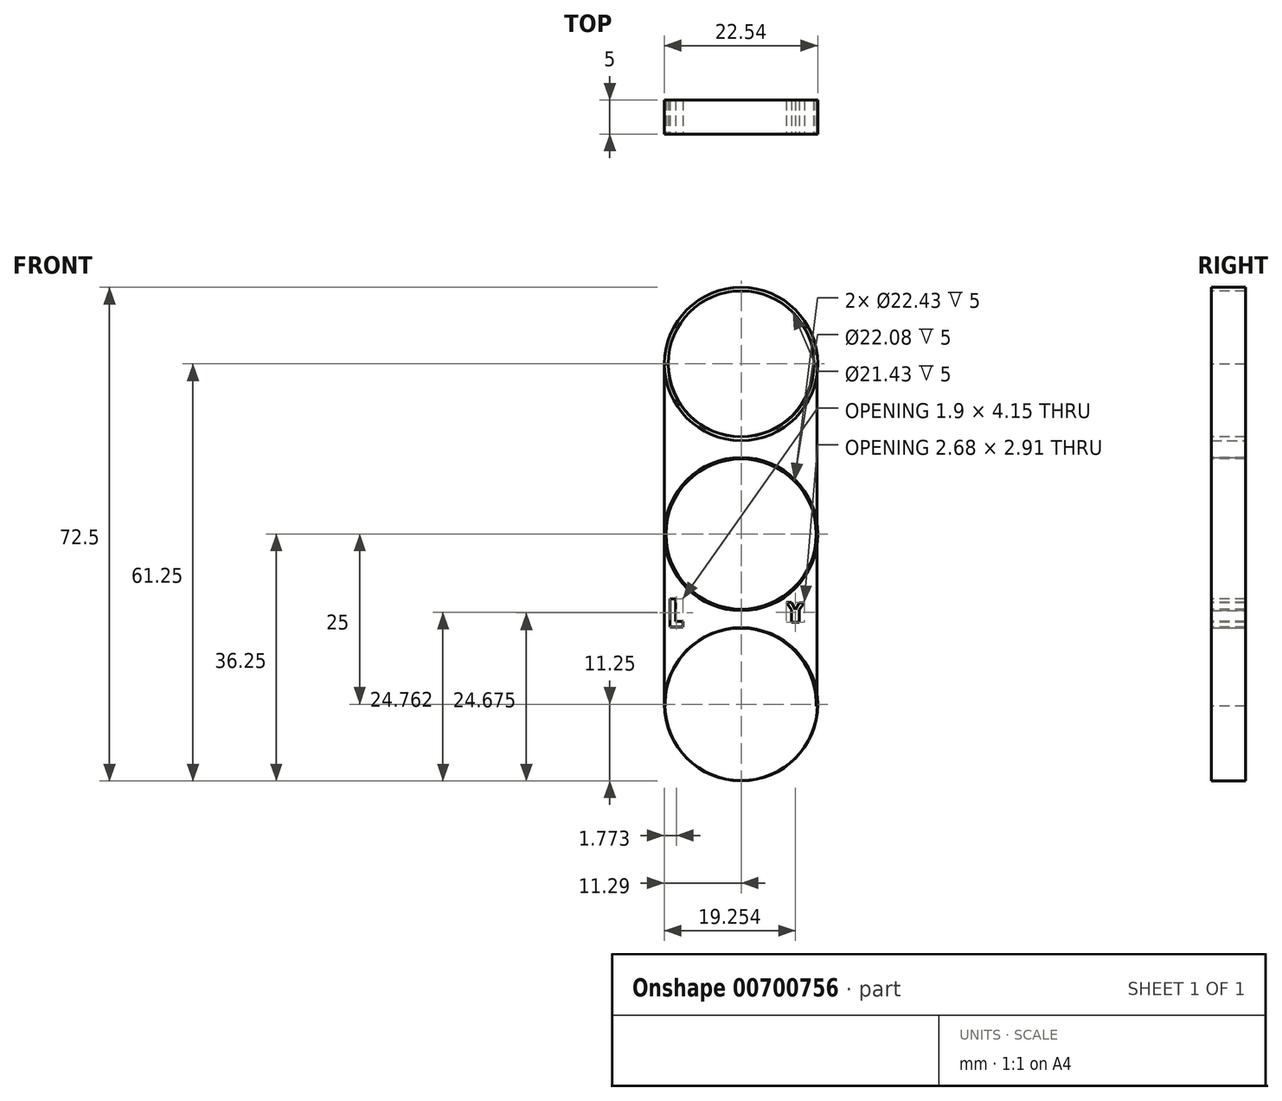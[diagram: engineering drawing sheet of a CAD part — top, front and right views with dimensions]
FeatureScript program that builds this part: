
annotation { "Feature Type Name" : "Feature", "Feature Type Description" : "" }
export const myFeature = defineFeature(function(context is Context, id is Id, definition is map)
    precondition{}
    {
        {
            var Q0;
            Q0=qCreatedBy(makeId("Front.planeOp"),FACE);
            var sketch = newSketch(context, id + "F0", { "sketchPlane" : qUnion([Q0])});
            skCircle(sketch, "E0", {"center": v(0, 25) * mm, "radius": 11.25 * mm});
            skCircle(sketch, "E1", {"center": v(0, 0) * mm, "radius": 11.25 * mm});
            skCircle(sketch, "E2", {"center": v(0, -25) * mm, "radius": 11.25 * mm});
            skSolve(sketch);
        }
        {
            var Q0;
            Q0=makeQuery(id+"F0.imprint","IMPRINT",FACE,{"disambiguationData":[TD([[makeQuery(id+"F0.imprint","IMPRINT",EDGE,{"derivedFrom":sQuery(id+"F0.wireOp",EDGE,"E0")}),1.0]])]});
            var Q1;
            Q1=makeQuery(id+"F0.imprint","IMPRINT",FACE,{"disambiguationData":[TD([[makeQuery(id+"F0.imprint","IMPRINT",EDGE,{"derivedFrom":sQuery(id+"F0.wireOp",EDGE,"E1")}),1.0]])]});
            var Q2;
            Q2=makeQuery(id+"F0.imprint","IMPRINT",FACE,{"disambiguationData":[TD([[makeQuery(id+"F0.imprint","IMPRINT",EDGE,{"derivedFrom":sQuery(id+"F0.wireOp",EDGE,"E2")}),1.0]])]});
            extrude(context, id + "F1", {"entities" : qUnion([Q0, Q1, Q2]), "depth" : 5 * mm, "offsetDistance" : 25 * mm});
        }
        {
            var Q0;
            Q0=makeQuery(id+"F1.opExtrude","CAP_FACE",FACE,{"disambiguationData":[OSD([sQuery(id+"F0.wireOp",EDGE,"E0")])],"isStart":false});
            var sketch = newSketch(context, id + "F2", { "sketchPlane" : qUnion([Q0])});
            skCircle(sketch, "E3", {"center": v(0, 25) * mm, "radius": 10.71 * mm});
            skSolve(sketch);
        }
        {
            var Q0;
            Q0=qSketchRegion(id+"F2",true);
            extrude(context, id + "F3", {"entities" : qUnion([Q0]), "operationType" : NewBodyOperationType.REMOVE, "oppositeDirection" : true, "depth" : 25 * mm, "offsetDistance" : 25 * mm});
        }
        {
            var Q0;
            Q0=makeQuery(id+"F1.opExtrude","CAP_FACE",FACE,{"disambiguationData":[OSD([sQuery(id+"F0.wireOp",EDGE,"E1")])],"isStart":false});
            var sketch = newSketch(context, id + "F4", { "sketchPlane" : qUnion([Q0])});
            skCircle(sketch, "E4", {"center": v(0, 0) * mm, "radius": 11.21 * mm});
            skSolve(sketch);
        }
        {
            var Q0;
            Q0=qSketchRegion(id+"F4",true);
            extrude(context, id + "F5", {"entities" : qUnion([Q0]), "operationType" : NewBodyOperationType.REMOVE, "oppositeDirection" : true, "depth" : 25 * mm, "offsetDistance" : 25 * mm});
        }
        {
            var Q0;
            Q0=makeQuery(id+"F1.opExtrude","CAP_FACE",FACE,{"disambiguationData":[OSD([sQuery(id+"F0.wireOp",EDGE,"E2")])],"isStart":false});
            var sketch = newSketch(context, id + "F6", { "sketchPlane" : qUnion([Q0])});
            skCircle(sketch, "E5", {"center": v(0, -25) * mm, "radius": 11.21 * mm});
            skSolve(sketch);
        }
        {
            var Q0;
            Q0=qSketchRegion(id+"F6",true);
            extrude(context, id + "F7", {"entities" : qUnion([Q0]), "operationType" : NewBodyOperationType.REMOVE, "oppositeDirection" : true, "depth" : 25 * mm, "offsetDistance" : 25 * mm});
        }
        {
            var Q0;
            Q0=qCreatedBy(makeId("Front.planeOp"),FACE);
            var sketch = newSketch(context, id + "F8", { "sketchPlane" : qUnion([Q0])});
            skLineSegment(sketch, "E6", {"start": v(-11.29, 24.95) * mm, "end": v(-11.29, -25.3) * mm});
            skLineSegment(sketch, "E7", {"start": v(11.15, 24.95) * mm, "end": v(11.15, -25.3) * mm});
            skLineSegment(sketch, "E8", {"start": v(-11.29, -25.3) * mm, "end": v(11.15, -25.3) * mm});
            skLineSegment(sketch, "E9", {"start": v(-11.29, 24.95) * mm, "end": v(11.15, 24.95) * mm});
            skSolve(sketch);
        }
        {
            var Q0;
            Q0=qSketchRegion(id+"F8",true);
            extrude(context, id + "F9", {"entities" : qUnion([Q0]), "depth" : 5 * mm, "offsetDistance" : 25 * mm});
        }
        {
            var Q0;
            Q0=makeQuery(id+"F9.opExtrude","CAP_FACE",FACE,{"disambiguationData":[OSD([sQuery(id+"F8.wireOp",EDGE,"E6"),sQuery(id+"F8.wireOp",EDGE,"E7"),sQuery(id+"F8.wireOp",EDGE,"E8"),sQuery(id+"F8.wireOp",EDGE,"E9")])],"isStart":false});
            var sketch = newSketch(context, id + "F10", { "sketchPlane" : qUnion([Q0])});
            skArc(sketch, "E10", {"start": v(-10.67, 24.95) * mm, "mid": v(-0.03, 14.3) * mm, "end": v(10.62, 24.95) * mm});
            skLineSegment(sketch, "E11", {"start": v(-10.67, 24.95) * mm, "end": v(10.62, 24.95) * mm});
            skSolve(sketch);
        }
        {
            var Q0;
            Q0=qSketchRegion(id+"F10",true);
            extrude(context, id + "F11", {"entities" : qUnion([Q0]), "operationType" : NewBodyOperationType.REMOVE, "oppositeDirection" : true, "depth" : 25 * mm, "offsetDistance" : 25 * mm});
        }
        {
            var Q0;
            Q0=makeQuery(id+"F9.opExtrude","CAP_FACE",FACE,{"disambiguationData":[OSD([sQuery(id+"F8.wireOp",EDGE,"E6"),sQuery(id+"F8.wireOp",EDGE,"E7"),sQuery(id+"F8.wireOp",EDGE,"E8"),sQuery(id+"F8.wireOp",EDGE,"E9")])],"isStart":false});
            var sketch = newSketch(context, id + "F12", { "sketchPlane" : qUnion([Q0])});
            skCircle(sketch, "E12", {"center": v(0, 0) * mm, "radius": 11.04 * mm});
            skSolve(sketch);
        }
        {
            var Q0;
            Q0=qSketchRegion(id+"F12",true);
            extrude(context, id + "F13", {"entities" : qUnion([Q0]), "operationType" : NewBodyOperationType.REMOVE, "oppositeDirection" : true, "depth" : 25 * mm, "offsetDistance" : 25 * mm});
        }
        {
            var Q0;
            Q0=makeQuery(id+"F9.opExtrude","CAP_FACE",FACE,{"disambiguationData":[OSD([sQuery(id+"F8.wireOp",EDGE,"E6"),sQuery(id+"F8.wireOp",EDGE,"E7"),sQuery(id+"F8.wireOp",EDGE,"E8"),sQuery(id+"F8.wireOp",EDGE,"E9")])],"isStart":false});
            var sketch = newSketch(context, id + "F14", { "sketchPlane" : qUnion([Q0])});
            skArc(sketch, "E13", {"start": v(11.02, -25.3) * mm, "mid": v(-0.07, -13.82) * mm, "end": v(-11.17, -25.3) * mm});
            skLineSegment(sketch, "E14", {"start": v(-11.17, -25.3) * mm, "end": v(11.02, -25.3) * mm});
            skSolve(sketch);
        }
        {
            var Q0;
            Q0=qSketchRegion(id+"F14",true);
            extrude(context, id + "F15", {"entities" : qUnion([Q0]), "operationType" : NewBodyOperationType.REMOVE, "oppositeDirection" : true, "depth" : 25 * mm, "offsetDistance" : 25 * mm});
        }
        {
            var Q0;
            Q0=makeQuery(id+"F9.opExtrude","CAP_FACE",FACE,{"disambiguationData":[OSD([sQuery(id+"F8.wireOp",EDGE,"E6"),sQuery(id+"F8.wireOp",EDGE,"E7"),sQuery(id+"F8.wireOp",EDGE,"E8"),sQuery(id+"F8.wireOp",EDGE,"E9")])],"isStart":false});
            var sketch = newSketch(context, id + "F16", { "sketchPlane" : qUnion([Q0])});
            skLineSegment(sketch, "E15", {"start": v(-10.47, -9.5) * mm, "end": v(-10.47, -13.65) * mm});
            skLineSegment(sketch, "E16", {"start": v(-10.47, -13.65) * mm, "end": v(-8.57, -13.65) * mm});
            skLineSegment(sketch, "E17", {"start": v(-8.57, -13.65) * mm, "end": v(-8.57, -12.82) * mm});
            skLineSegment(sketch, "E18", {"start": v(-8.57, -12.82) * mm, "end": v(-9.6, -12.82) * mm});
            skLineSegment(sketch, "E19", {"start": v(-9.6, -12.82) * mm, "end": v(-9.6, -9.5) * mm});
            skLineSegment(sketch, "E20", {"start": v(-9.6, -9.5) * mm, "end": v(-10.47, -9.5) * mm});
            skSolve(sketch);
        }
        {
            var Q0;
            Q0=qSketchRegion(id+"F16",true);
            extrude(context, id + "F17", {"entities" : qUnion([Q0]), "operationType" : NewBodyOperationType.REMOVE, "oppositeDirection" : true, "depth" : 25 * mm, "offsetDistance" : 25 * mm});
        }
        {
            var Q0;
            Q0=makeQuery(id+"F9.opExtrude","CAP_FACE",FACE,{"disambiguationData":[OSD([sQuery(id+"F8.wireOp",EDGE,"E6"),sQuery(id+"F8.wireOp",EDGE,"E7"),sQuery(id+"F8.wireOp",EDGE,"E8"),sQuery(id+"F8.wireOp",EDGE,"E9")])],"isStart":false});
            var sketch = newSketch(context, id + "F18", { "sketchPlane" : qUnion([Q0])});
            skLineSegment(sketch, "E21", {"start": v(6.62, -10.04) * mm, "end": v(7.4, -10.04) * mm});
            skLineSegment(sketch, "E22", {"start": v(7.4, -10.04) * mm, "end": v(7.96, -11.1) * mm});
            skLineSegment(sketch, "E23", {"start": v(7.96, -11.1) * mm, "end": v(8.52, -10.1) * mm});
            skLineSegment(sketch, "E24", {"start": v(8.52, -10.1) * mm, "end": v(9.3, -10.1) * mm});
            skLineSegment(sketch, "E25", {"start": v(9.3, -10.1) * mm, "end": v(8.52, -11.1) * mm});
            skLineSegment(sketch, "E26", {"start": v(8.52, -11.1) * mm, "end": v(8.52, -12.94) * mm});
            skLineSegment(sketch, "E27", {"start": v(8.52, -12.94) * mm, "end": v(7.4, -12.94) * mm});
            skLineSegment(sketch, "E28", {"start": v(7.4, -12.94) * mm, "end": v(7.4, -11.1) * mm});
            skLineSegment(sketch, "E29", {"start": v(7.4, -11.1) * mm, "end": v(6.62, -10.04) * mm});
            skSolve(sketch);
        }
        {
            var Q0;
            Q0=qSketchRegion(id+"F18",true);
            extrude(context, id + "F19", {"entities" : qUnion([Q0]), "operationType" : NewBodyOperationType.REMOVE, "oppositeDirection" : true, "depth" : 25 * mm, "offsetDistance" : 25 * mm});
        }
    });
